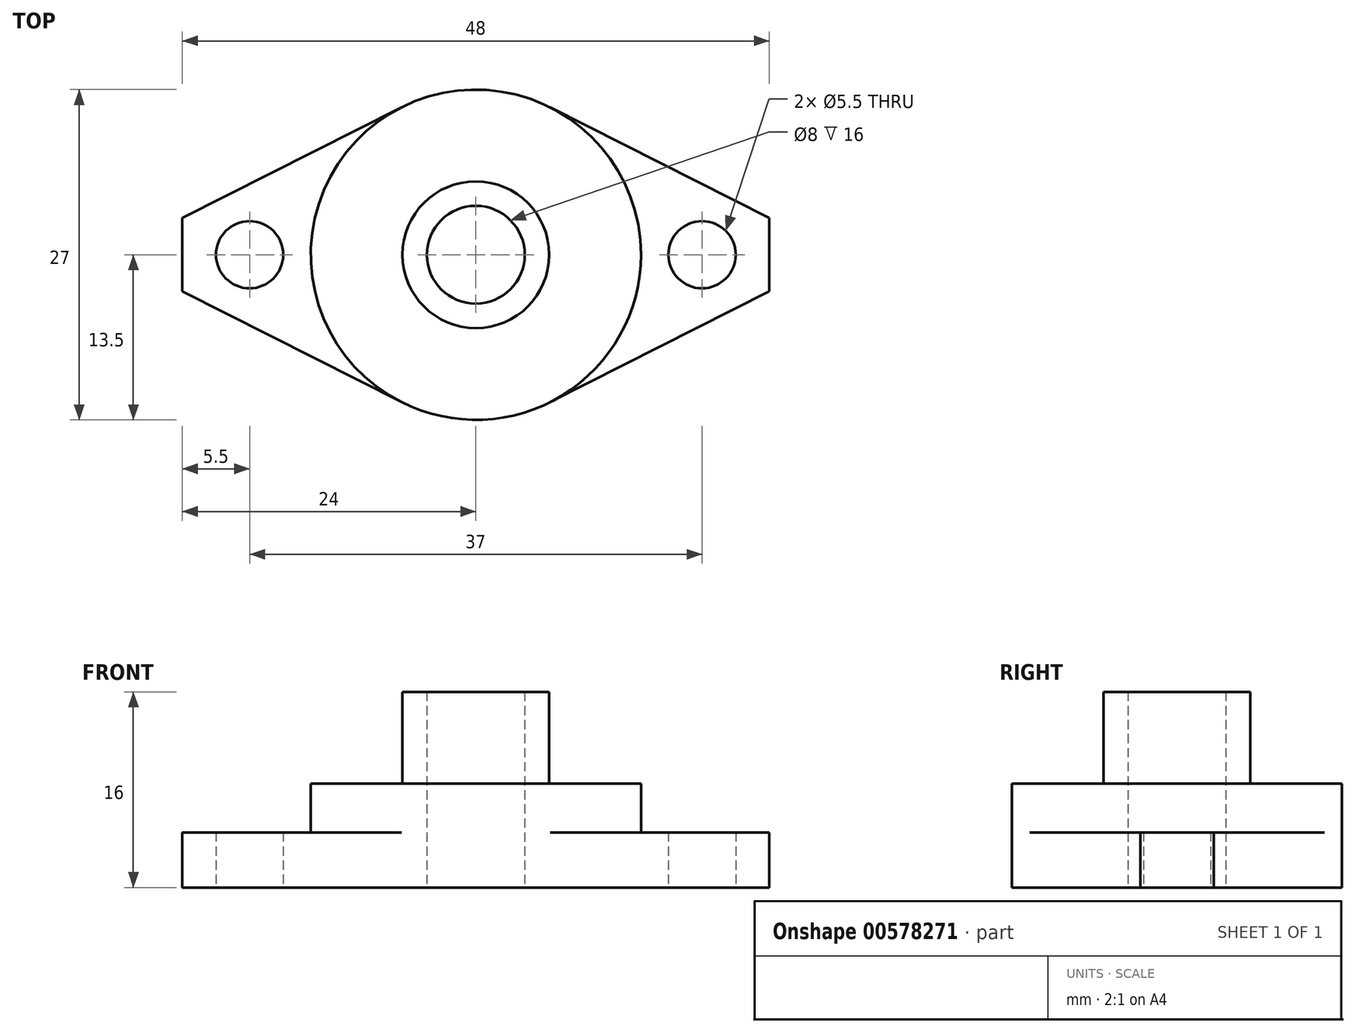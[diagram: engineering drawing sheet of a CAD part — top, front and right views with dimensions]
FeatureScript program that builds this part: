
annotation { "Feature Type Name" : "Feature", "Feature Type Description" : "" }
export const myFeature = defineFeature(function(context is Context, id is Id, definition is map)
    precondition{}
    {
        {
            var Q0;
            Q0=qCreatedBy(makeId("Top.planeOp"),FACE);
            var sketch = newSketch(context, id + "F0", { "sketchPlane" : qUnion([Q0])});
            skCircle(sketch, "E0", {"center": v(0, 0) * mm, "radius": 13.5 * mm});
            skCircle(sketch, "E1", {"center": v(0, 0) * mm, "radius": 4 * mm});
            skCircle(sketch, "E2", {"center": v(18.5, 0) * mm, "radius": 2.75 * mm});
            skCircle(sketch, "E3", {"center": v(-18.5, 0) * mm, "radius": 2.75 * mm});
            skLineSegment(sketch, "E4", {"start": v(-6.09, 12.05) * mm, "end": v(-24, 3) * mm});
            skLineSegment(sketch, "E5.MirrorCS", {"start": v(-6.09, -12.05) * mm, "end": v(-24, -3) * mm});
            skLineSegment(sketch, "E6", {"start": v(-24, 3) * mm, "end": v(-24, -3) * mm});
            skLineSegment(sketch, "E7.MirrorCS", {"start": v(6.09, 12.05) * mm, "end": v(24, 3) * mm});
            skLineSegment(sketch, "E8.MirrorCS", {"start": v(24, 3) * mm, "end": v(24, -3) * mm});
            skLineSegment(sketch, "E9.MirrorCS", {"start": v(6.09, -12.05) * mm, "end": v(24, -3) * mm});
            skLineSegment(sketch, "E10", {"start": v(-24, 0) * mm, "end": v(24, 0) * mm});
            skSolve(sketch);
        }
        {
            var Q0;
            Q0=makeQuery(id+"F0.imprint","IMPRINT",FACE,{"disambiguationData":[TD([[makeQuery(id+"F0.imprint","IMPRINT",EDGE,{"derivedFrom":sQuery(id+"F0.wireOp",EDGE,"E1")}),-1.0]])]});
            extrude(context, id + "F1", {"entities" : qUnion([Q0]), "depth" : 16 * mm, "offsetDistance" : 25 * mm});
        }
        {
            var Q0;
            Q0=makeQuery(id+"F0.imprint","IMPRINT",FACE,{"disambiguationData":[TD([[makeQuery(id+"F0.imprint","IMPRINT",EDGE,{"derivedFrom":sQuery(id+"F0.wireOp",EDGE,"E3")}),-1.0]])]});
            var Q1;
            Q1=makeQuery(id+"F0.imprint","IMPRINT",FACE,{"disambiguationData":[TD([[makeQuery(id+"F0.imprint","IMPRINT",EDGE,{"derivedFrom":sQuery(id+"F0.wireOp",EDGE,"E2")}),-1.0]])]});
            extrude(context, id + "F2", {"entities" : qUnion([Q0, Q1]), "operationType" : NewBodyOperationType.ADD, "depth" : 4.5 * mm, "offsetDistance" : 25 * mm});
        }
        {
            var Q0;
            Q0=makeQuery(id+"F1.opExtrude","CAP_FACE",FACE,{"disambiguationData":[OSD([sQuery(id+"F0.wireOp",EDGE,"E0"),sQuery(id+"F0.wireOp",EDGE,"E1")])],"isStart":false});
            var sketch = newSketch(context, id + "F3", { "sketchPlane" : qUnion([Q0])});
            skCircle(sketch, "E11", {"center": v(0, 0) * mm, "radius": 6 * mm});
            skSolve(sketch);
        }
        {
            var Q0;
            Q0=makeQuery(id+"F3.imprint","IMPRINT",FACE,{"disambiguationData":[TD([[makeQuery(id+"F3.imprint","IMPRINT",EDGE,{"derivedFrom":sQuery(id+"F3.wireOp",EDGE,"E11")}),-1.0]])]});
            extrude(context, id + "F4", {"entities" : qUnion([Q0]), "operationType" : NewBodyOperationType.REMOVE, "oppositeDirection" : true, "depth" : 7.5 * mm, "offsetDistance" : 25 * mm});
        }
    });
